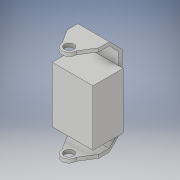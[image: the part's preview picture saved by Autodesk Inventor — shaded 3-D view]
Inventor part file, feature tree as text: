
AUTODESK INVENTOR PART (.ipt)
format: ipt  version: 2018 (Build 220112000, 112)  size: 185,344 bytes
history: native  units: mm
features: extrude x6, sketch x6
ambient origin geometry x8: Origin, YZ Plane, XZ Plane, XY Plane, X Axis, Y Axis, Z Axis, Center Point
bodies: Solid1 (feature_tree)
feature tree (12):
  extrude  "Extrusion1"  Depth=12.0mm
  extrude  "Extrusion2"  Depth=13.5mm
  extrude  "Extrusion3"  Depth=27.0mm
  extrude  "Extrusion4"  Depth=3.0mm TaperAngle=0.0deg
  extrude  "Extrusion5"  Depth=3.0mm
  extrude  "Extrusion6"  Depth=4.0mm TaperAngle=0.0deg
  sketch  "Sketch1"  dims[d0=8.0mm d1=12.0mm]
  sketch  "Sketch2"  dims[d2=21.0mm d3=13.5mm]
  sketch  "Sketch3"  dims[d4=27.0mm d5=9.0mm]
  sketch  "Sketch4"  dims[d6=9.0mm d7=3.0mm d8=0.0mm]
  sketch  "Sketch5"  dims[d11=60.0mm d14=3.0mm]
  sketch  "Sketch6"  dims[d16=27.0mm d17=0.0mm d18=45.0mm d19=0.0mm d20=1.254mm d21=17.5mm d22=48.0mm d23=35.0mm d24=26.0mm d25=0.0mm d28=8.0mm d29=10.0mm d30=0.0mm d34=8.0mm d35=12.0mm d36=4.0mm d37=0.0mm]
